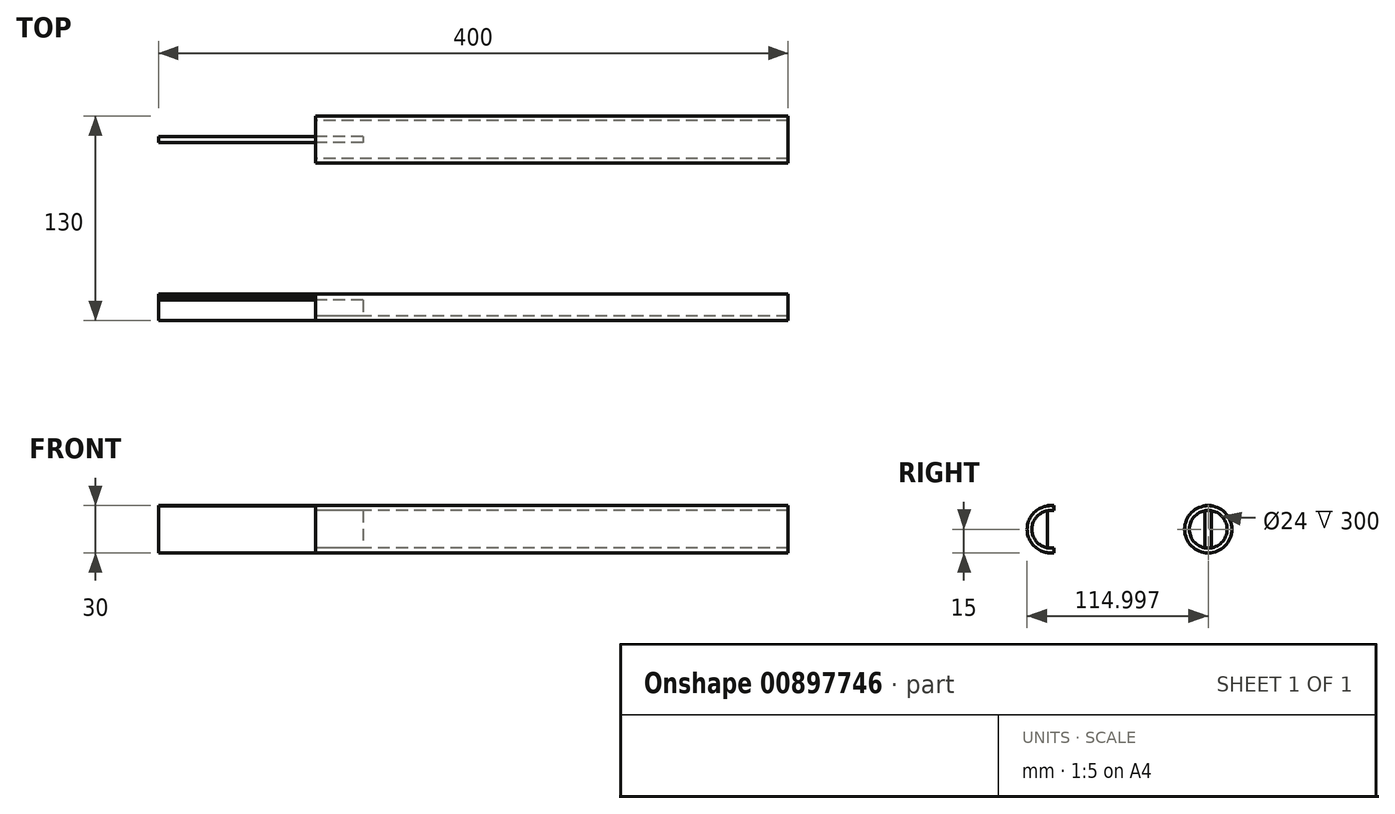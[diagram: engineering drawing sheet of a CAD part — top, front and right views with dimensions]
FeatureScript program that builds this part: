
annotation { "Feature Type Name" : "Feature", "Feature Type Description" : "" }
export const myFeature = defineFeature(function(context is Context, id is Id, definition is map)
    precondition{}
    {
        {
            var Q0;
            Q0=qCreatedBy(makeId("Right.planeOp"),FACE);
            var sketch = newSketch(context, id + "F0", { "sketchPlane" : qUnion([Q0])});
            skCircle(sketch, "E0", {"center": v(-31.6, 0) * mm, "radius": 15 * mm});
            skCircle(sketch, "E1", {"center": v(68.4, 0) * mm, "radius": 15 * mm});
            skCircle(sketch, "E2", {"center": v(68.4, 0) * mm, "radius": 12 * mm});
            skCircle(sketch, "E3", {"center": v(-31.6, 0) * mm, "radius": 12 * mm});
            skLineSegment(sketch, "E4.bottom", {"start": v(-29.6, -15) * mm, "end": v(-33.6, -15) * mm});
            skLineSegment(sketch, "E4.top", {"start": v(-29.6, 15) * mm, "end": v(-33.6, 15) * mm});
            skLineSegment(sketch, "E4.left", {"start": v(-29.6, -15) * mm, "end": v(-29.6, 15) * mm});
            skLineSegment(sketch, "E4.right", {"start": v(-33.6, -15) * mm, "end": v(-33.6, 15) * mm});
            skLineSegment(sketch, "E5.bottom", {"start": v(66.4, 15) * mm, "end": v(70.4, 15) * mm});
            skLineSegment(sketch, "E5.top", {"start": v(66.4, -15) * mm, "end": v(70.4, -15) * mm});
            skLineSegment(sketch, "E5.left", {"start": v(66.4, 15) * mm, "end": v(66.4, -15) * mm});
            skLineSegment(sketch, "E5.right", {"start": v(70.4, 15) * mm, "end": v(70.4, -15) * mm});
            skSolve(sketch);
        }
        {
            var Q0;
            {var subQ0=sQuery(id+"F0.wireOp",EDGE,"E5.left");var subQ1=sQuery(id+"F0.wireOp",EDGE,"E2");var subQ2=makeQuery(id+"F0.imprint","INTERSECT",VERTEX,{"disambiguationData":[OD(0.0)],"derivedFrom":[subQ1,subQ0]});Q0=makeQuery(id+"F0.imprint","IMPRINT",FACE,{"disambiguationData":[TD([[makeQuery(id+"F0.imprint","IMPRINT",EDGE,{"disambiguationData":[TD([[subQ2,1.0]])],"derivedFrom":subQ1}),1.0]])]});}
            var Q1;
            {var subQ5=sQuery(id+"F0.wireOp",EDGE,"E5.top");Q1=makeQuery(id+"F0.imprint","IMPRINT",FACE,{"disambiguationData":[TD([[makeQuery(id+"F0.imprint","IMPRINT",EDGE,{"derivedFrom":subQ5}),1.0]])]});}
            var Q2;
            {var subQ0=sQuery(id+"F0.wireOp",EDGE,"E5.left");var subQ1=sQuery(id+"F0.wireOp",EDGE,"E1");var subQ2=makeQuery(id+"F0.imprint","INTERSECT",VERTEX,{"disambiguationData":[OD(1.0)],"derivedFrom":[subQ1,subQ0]});Q2=makeQuery(id+"F0.imprint","IMPRINT",FACE,{"disambiguationData":[TD([[makeQuery(id+"F0.imprint","IMPRINT",EDGE,{"disambiguationData":[TD([[subQ2,-1.0]])],"derivedFrom":subQ1}),1.0]])]});}
            var Q3;
            {var subQ0=sQuery(id+"F0.wireOp",EDGE,"E5.left");var subQ1=sQuery(id+"F0.wireOp",EDGE,"E1");var subQ2=makeQuery(id+"F0.imprint","INTERSECT",VERTEX,{"disambiguationData":[OD(0.0)],"derivedFrom":[subQ1,subQ0]});Q3=makeQuery(id+"F0.imprint","IMPRINT",FACE,{"disambiguationData":[TD([[makeQuery(id+"F0.imprint","IMPRINT",EDGE,{"disambiguationData":[TD([[subQ2,1.0]])],"derivedFrom":subQ1}),1.0]])]});}
            var Q4;
            {var subQ5=sQuery(id+"F0.wireOp",EDGE,"E5.bottom");Q4=makeQuery(id+"F0.imprint","IMPRINT",FACE,{"disambiguationData":[TD([[makeQuery(id+"F0.imprint","IMPRINT",EDGE,{"derivedFrom":subQ5}),-1.0]])]});}
            var Q5;
            {var subQ5=sQuery(id+"F0.wireOp",EDGE,"E4.top");Q5=makeQuery(id+"F0.imprint","IMPRINT",FACE,{"disambiguationData":[TD([[makeQuery(id+"F0.imprint","IMPRINT",EDGE,{"derivedFrom":subQ5}),1.0]])]});}
            var Q6;
            {var subQ0=sQuery(id+"F0.wireOp",EDGE,"E4.right");var subQ1=sQuery(id+"F0.wireOp",EDGE,"E0");var subQ2=makeQuery(id+"F0.imprint","INTERSECT",VERTEX,{"disambiguationData":[OD(0.0)],"derivedFrom":[subQ1,subQ0]});Q6=makeQuery(id+"F0.imprint","IMPRINT",FACE,{"disambiguationData":[TD([[makeQuery(id+"F0.imprint","IMPRINT",EDGE,{"disambiguationData":[TD([[subQ2,1.0]])],"derivedFrom":subQ1}),1.0]])]});}
            var Q7;
            {var subQ0=sQuery(id+"F0.wireOp",EDGE,"E4.right");var subQ1=sQuery(id+"F0.wireOp",EDGE,"E3");var subQ2=makeQuery(id+"F0.imprint","INTERSECT",VERTEX,{"disambiguationData":[OD(0.0)],"derivedFrom":[subQ1,subQ0]});Q7=makeQuery(id+"F0.imprint","IMPRINT",FACE,{"disambiguationData":[TD([[makeQuery(id+"F0.imprint","IMPRINT",EDGE,{"disambiguationData":[TD([[subQ2,1.0]])],"derivedFrom":subQ1}),1.0]])]});}
            var Q8;
            {var subQ0=sQuery(id+"F0.wireOp",EDGE,"E4.right");var subQ1=sQuery(id+"F0.wireOp",EDGE,"E0");var subQ2=makeQuery(id+"F0.imprint","INTERSECT",VERTEX,{"disambiguationData":[OD(1.0)],"derivedFrom":[subQ1,subQ0]});Q8=makeQuery(id+"F0.imprint","IMPRINT",FACE,{"disambiguationData":[TD([[makeQuery(id+"F0.imprint","IMPRINT",EDGE,{"disambiguationData":[TD([[subQ2,-1.0]])],"derivedFrom":subQ1}),1.0]])]});}
            var Q9;
            {var subQ5=sQuery(id+"F0.wireOp",EDGE,"E4.bottom");Q9=makeQuery(id+"F0.imprint","IMPRINT",FACE,{"disambiguationData":[TD([[makeQuery(id+"F0.imprint","IMPRINT",EDGE,{"derivedFrom":subQ5}),-1.0]])]});}
            extrude(context, id + "F1", {"entities" : qUnion([Q0, Q1, Q2, Q3, Q4, Q5, Q6, Q7, Q8, Q9]), "oppositeDirection" : true, "depth" : 100 * mm, "offsetDistance" : 25.4 * mm});
        }
        {
            var Q0;
            {var subQ0=sQuery(id+"F0.wireOp",EDGE,"E5.right");var subQ1=sQuery(id+"F0.wireOp",EDGE,"E1");var subQ2=makeQuery(id+"F0.imprint","INTERSECT",VERTEX,{"disambiguationData":[OD(0.0)],"derivedFrom":[subQ1,subQ0]});Q0=makeQuery(id+"F0.imprint","IMPRINT",FACE,{"disambiguationData":[TD([[makeQuery(id+"F0.imprint","IMPRINT",EDGE,{"disambiguationData":[TD([[subQ2,1.0]])],"derivedFrom":subQ1}),1.0]])]});}
            var Q1;
            {var subQ1=sQuery(id+"F0.wireOp",EDGE,"E1");var subQ5=makeQuery(id+"F0.imprint","INTERSECT",VERTEX,{"derivedFrom":[subQ1,sQuery(id+"F0.wireOp",EDGE,"E5.bottom")]});Q1=makeQuery(id+"F0.imprint","IMPRINT",FACE,{"disambiguationData":[TD([[makeQuery(id+"F0.imprint","IMPRINT",EDGE,{"disambiguationData":[TD([[subQ5,1.0]])],"derivedFrom":subQ1}),1.0]])]});}
            var Q2;
            {var subQ0=sQuery(id+"F0.wireOp",EDGE,"E5.left");var subQ1=sQuery(id+"F0.wireOp",EDGE,"E1");var subQ2=makeQuery(id+"F0.imprint","INTERSECT",VERTEX,{"disambiguationData":[OD(0.0)],"derivedFrom":[subQ1,subQ0]});Q2=makeQuery(id+"F0.imprint","IMPRINT",FACE,{"disambiguationData":[TD([[makeQuery(id+"F0.imprint","IMPRINT",EDGE,{"disambiguationData":[TD([[subQ2,-1.0]])],"derivedFrom":subQ1}),1.0]])]});}
            var Q3;
            {var subQ0=sQuery(id+"F0.wireOp",EDGE,"E5.left");var subQ1=sQuery(id+"F0.wireOp",EDGE,"E1");var subQ2=makeQuery(id+"F0.imprint","INTERSECT",VERTEX,{"disambiguationData":[OD(1.0)],"derivedFrom":[subQ1,subQ0]});Q3=makeQuery(id+"F0.imprint","IMPRINT",FACE,{"disambiguationData":[TD([[makeQuery(id+"F0.imprint","IMPRINT",EDGE,{"disambiguationData":[TD([[subQ2,-1.0]])],"derivedFrom":subQ1}),1.0]])]});}
            var Q4;
            {var subQ0=sQuery(id+"F0.wireOp",EDGE,"E4.right");var subQ1=sQuery(id+"F0.wireOp",EDGE,"E0");var subQ2=makeQuery(id+"F0.imprint","INTERSECT",VERTEX,{"disambiguationData":[OD(0.0)],"derivedFrom":[subQ1,subQ0]});Q4=makeQuery(id+"F0.imprint","IMPRINT",FACE,{"disambiguationData":[TD([[makeQuery(id+"F0.imprint","IMPRINT",EDGE,{"disambiguationData":[TD([[subQ2,-1.0]])],"derivedFrom":subQ1}),1.0]])]});}
            var Q5;
            {var subQ1=sQuery(id+"F0.wireOp",EDGE,"E0");var subQ7=makeQuery(id+"F0.imprint","INTERSECT",VERTEX,{"derivedFrom":[subQ1,sQuery(id+"F0.wireOp",EDGE,"E4.top")]});Q5=makeQuery(id+"F0.imprint","IMPRINT",FACE,{"disambiguationData":[TD([[makeQuery(id+"F0.imprint","IMPRINT",EDGE,{"disambiguationData":[TD([[subQ7,1.0]])],"derivedFrom":subQ1}),1.0]])]});}
            var Q6;
            {var subQ0=sQuery(id+"F0.wireOp",EDGE,"E4.left");var subQ1=sQuery(id+"F0.wireOp",EDGE,"E0");var subQ2=makeQuery(id+"F0.imprint","INTERSECT",VERTEX,{"disambiguationData":[OD(0.0)],"derivedFrom":[subQ1,subQ0]});Q6=makeQuery(id+"F0.imprint","IMPRINT",FACE,{"disambiguationData":[TD([[makeQuery(id+"F0.imprint","IMPRINT",EDGE,{"disambiguationData":[TD([[subQ2,1.0]])],"derivedFrom":subQ1}),1.0]])]});}
            var Q7;
            {var subQ1=sQuery(id+"F0.wireOp",EDGE,"E0");var subQ5=sQuery(id+"F0.wireOp",EDGE,"E4.right");var subQ6=makeQuery(id+"F0.imprint","INTERSECT",VERTEX,{"disambiguationData":[OD(1.0)],"derivedFrom":[subQ1,subQ5]});Q7=makeQuery(id+"F0.imprint","IMPRINT",FACE,{"disambiguationData":[TD([[makeQuery(id+"F0.imprint","IMPRINT",EDGE,{"disambiguationData":[TD([[subQ6,-1.0]])],"derivedFrom":subQ1}),1.0]])]});}
            extrude(context, id + "F2", {"entities" : qUnion([Q0, Q1, Q2, Q3, Q4, Q5, Q6, Q7]), "depth" : 300 * mm, "offsetDistance" : 25.4 * mm});
        }
        {
            var Q0;
            {var subQ0=sQuery(id+"F0.wireOp",EDGE,"E5.left");var subQ1=sQuery(id+"F0.wireOp",EDGE,"E2");var subQ2=makeQuery(id+"F0.imprint","INTERSECT",VERTEX,{"disambiguationData":[OD(0.0)],"derivedFrom":[subQ1,subQ0]});Q0=makeQuery(id+"F0.imprint","IMPRINT",FACE,{"disambiguationData":[TD([[makeQuery(id+"F0.imprint","IMPRINT",EDGE,{"disambiguationData":[TD([[subQ2,1.0]])],"derivedFrom":subQ1}),1.0]])]});}
            var Q1;
            {var subQ0=sQuery(id+"F0.wireOp",EDGE,"E4.right");var subQ1=sQuery(id+"F0.wireOp",EDGE,"E3");var subQ2=makeQuery(id+"F0.imprint","INTERSECT",VERTEX,{"disambiguationData":[OD(0.0)],"derivedFrom":[subQ1,subQ0]});Q1=makeQuery(id+"F0.imprint","IMPRINT",FACE,{"disambiguationData":[TD([[makeQuery(id+"F0.imprint","IMPRINT",EDGE,{"disambiguationData":[TD([[subQ2,1.0]])],"derivedFrom":subQ1}),1.0]])]});}
            extrude(context, id + "F3", {"entities" : qUnion([Q0, Q1]), "depth" : 30 * mm, "offsetDistance" : 25.4 * mm});
        }
    });
